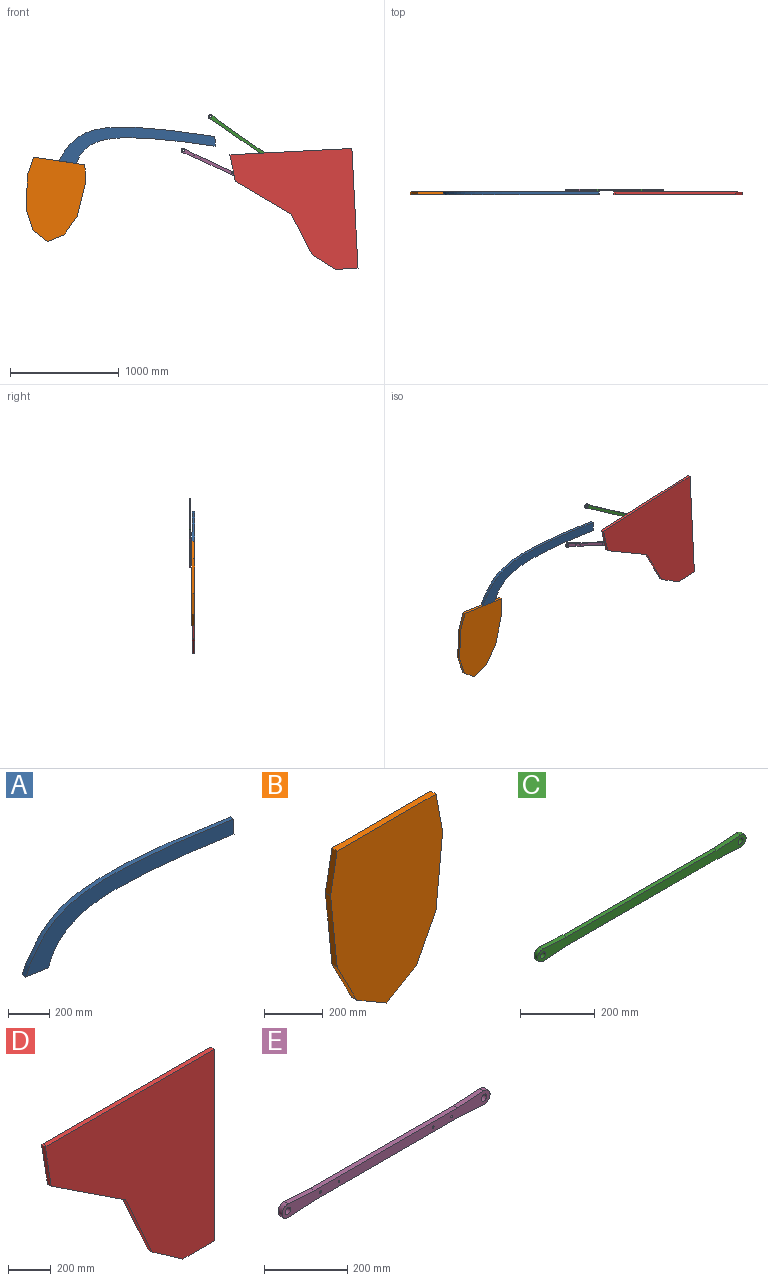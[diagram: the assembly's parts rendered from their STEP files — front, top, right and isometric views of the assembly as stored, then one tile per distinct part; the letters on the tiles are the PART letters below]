
ASSEMBLY  parts=5 mates=4
PART A: 7 faces, bbox 1432.8x25x381.3 mm
  f0: extruded ~999.54x237.45mm, area 27511.2mm2, adj f1,f4,f5,f6
  f1: extruded ~274.97x38.74mm, area 6942.4mm2, adj f0,f2,f5,f6
  f2: plane 90x25mm, normal (1,0,0), area 2250mm2, adj f1,f3,f5,f6
  f3: extruded ~1432.68x311.07mm, area 39088.2mm2, adj f2,f4,f5,f6
  f4: plane 158.25x25mm, normal (-0.15,0,-0.99), area 4000mm2, adj f0,f3,f5,f6
  f5: plane 1432.77x381.26mm, normal (0,-1,0), area 152801.9mm2, adj f0,f1,f2,f3,f4
  f6: plane 1432.77x381.26mm, normal (0,1,0), area 152801.9mm2, adj f0,f1,f2,f3,f4
PART B: 11 faces, bbox 538.6x25x751.3 mm
  f0: plane 475.91x25mm, normal (0,0,1), area 11897.7mm2, adj f1,f8,f9,f10
  f1: plane 170.47x31.37mm, normal (-0.98,0,0.18), area 4333.3mm2, adj f0,f2,f9,f10
  f2: plane 313.48x31.84mm, normal (-0.99,0,-0.1), area 7877.4mm2, adj f1,f3,f9,f10
  f3: plane 183.96x94.35mm, normal (-0.89,0,-0.46), area 5168.8mm2, adj f2,f4,f9,f10
  f4: plane 143.13x83.43mm, normal (-0.5,0,-0.86), area 4141.8mm2, adj f3,f5,f9,f10
  f5: plane 143.13x83.43mm, normal (0.5,0,-0.86), area 4141.8mm2, adj f4,f6,f9,f10
  f6: plane 183.96x94.35mm, normal (0.89,0,-0.46), area 5168.8mm2, adj f5,f7,f9,f10
  f7: plane 313.48x31.84mm, normal (0.99,0,-0.1), area 7877.4mm2, adj f6,f8,f9,f10
  f8: plane 170.47x31.37mm, normal (0.98,0,0.18), area 4333.3mm2, adj f0,f7,f9,f10
  f9: plane 751.35x538.64mm, normal (0,-1,0), area 327311.6mm2, adj f0,f1,f2,f3,f4,f5,f6,f7
  f10: plane 751.35x538.64mm, normal (0,1,0), area 327311.6mm2, adj f0,f1,f2,f3,f4,f5,f6,f7
PART C: 12 faces, bbox 790x14x40 mm
  f0: plane 88.77x14mm, normal (0.06,0,1), area 1245.2mm2, adj f1,f8,f10,f11
  f1: cylinder r=20mm len=40mm, axis (0,1,0), area 914.1mm2, adj f0,f2,f10,f11
  f2: plane 88.77x14mm, normal (0.06,0,-1), area 1245.2mm2, adj f1,f3,f10,f11
  f3: plane 570x14mm, normal (0,0,-1), area 7980mm2, adj f2,f4,f10,f11
  f4: plane 88.77x14mm, normal (-0.06,0,-1), area 1245.2mm2, adj f3,f5,f10,f11
  f5: cylinder r=20mm len=40mm, axis (0,1,0), area 914.1mm2, adj f4,f6,f10,f11
  f6: plane 88.77x14mm, normal (-0.06,0,1), area 1245.2mm2, adj f5,f8,f10,f11
  f7: cylinder r=9.5mm len=19mm, axis (0,1,0), area 835.7mm2, adj f10,f11
  f8: plane 570x14mm, normal (0,0,1), area 7980mm2, adj f0,f6,f10,f11
  f9: cylinder r=9.5mm len=19mm, axis (0,1,0), area 835.7mm2, adj f10,f11
  f10: plane 790x40mm, normal (0,-1,0), area 23436.3mm2, adj f0,f1,f2,f3,f4,f5,f6,f7
  f11: plane 790x40mm, normal (0,1,0), area 23436.3mm2, adj f0,f1,f2,f3,f4,f5,f6,f7
PART D: 14 faces, bbox 1125.3x50x1103.2 mm
  f0: plane 1112.1x25mm, normal (0,0,1), area 27802.5mm2, adj f1,f7,f8,f9
  f1: plane 25x13.25mm, normal (0.04,0,1), area 331.5mm2, adj f0,f2,f8,f9
  f2: plane 246.31x39.73mm, normal (-0.99,0,-0.16), area 6237.4mm2, adj f1,f3,f8,f9
  f3: plane 493.74x325.38mm, normal (-0.55,0,-0.83), area 14782.7mm2, adj f2,f4,f8,f9
  f4: plane 387.83x175.82mm, normal (-0.91,0,-0.41), area 10645.6mm2, adj f3,f5,f8,f9
  f5: plane 205.99x143.68mm, normal (-0.57,0,-0.82), area 6278.8mm2, adj f4,f6,f8,f9
  f6: plane 210.07x25mm, normal (0,0,-1), area 5251.8mm2, adj f5,f7,f8,f9
  f7: plane 1103.2x25mm, normal (1,0,0), area 27580.1mm2, adj f0,f6,f8,f9
  f8: plane 1125.35x1103.2mm, normal (0,-1,0), area 785366.9mm2, adj f0,f1,f2,f3,f4,f5,f6,f7
  f9: plane 1125.35x1103.2mm, normal (0,1,0), area 784799.8mm2, adj f0,f1,f2,f3,f4,f5,f6,f7
  f10: plane 19x19mm, normal (0,1,0), area 283.5mm2, adj f11
  f11: cylinder r=9.5mm len=25mm, axis (0,-1,0), area 1492.3mm2, adj f9,f10
  f12: plane 19x19mm, normal (0,1,0), area 283.5mm2, adj f13
  f13: cylinder r=9.5mm len=25mm, axis (0,-1,0), area 1492.3mm2, adj f9,f12
PART E: 16 faces, bbox 706.7x14x40 mm
  f0: plane 88.77x14mm, normal (0.06,0,1), area 1245.2mm2, adj f1,f12,f14,f15
  f1: cylinder r=20mm len=40mm, axis (0,1,0), area 914.1mm2, adj f0,f2,f14,f15
  f2: plane 88.77x14mm, normal (0.06,0,-1), area 1245.2mm2, adj f1,f3,f14,f15
  f3: plane 486.7x14mm, normal (0,0,-1), area 6813.8mm2, adj f2,f4,f14,f15
  f4: plane 88.77x14mm, normal (-0.06,0,-1), area 1245.2mm2, adj f3,f5,f14,f15
  f5: cylinder r=20mm len=40mm, axis (0,1,0), area 914.1mm2, adj f4,f6,f14,f15
  f6: plane 88.77x14mm, normal (-0.06,0,1), area 1245.2mm2, adj f5,f12,f14,f15
  f7: cylinder r=3.2mm len=14mm, axis (0,1,0), area 281.5mm2, adj f14,f15
  f8: cylinder r=3.2mm len=14mm, axis (0,1,0), area 281.5mm2, adj f14,f15
  f9: cylinder r=3.2mm len=14mm, axis (0,1,0), area 281.5mm2, adj f14,f15
  f10: cylinder r=3.2mm len=14mm, axis (0,1,0), area 281.5mm2, adj f14,f15
  f11: cylinder r=9.5mm len=19mm, axis (0,1,0), area 835.7mm2, adj f14,f15
  f12: plane 486.7x14mm, normal (0,0,1), area 6813.8mm2, adj f0,f6,f14,f15
  f13: cylinder r=9.5mm len=19mm, axis (0,1,0), area 835.7mm2, adj f14,f15
  f14: plane 706.7x40mm, normal (0,-1,0), area 20891.9mm2, adj f0,f1,f2,f3,f4,f5,f6,f7
  f15: plane 706.7x40mm, normal (0,1,0), area 20891.9mm2, adj f0,f1,f2,f3,f4,f5,f6,f7
PLACE A t=(0,57.54,0)mm
PLACE B rot(axis=(0,1,0),8.5deg) t=(-2523.72,57.54,183.3)mm
PLACE C rot(axis=(0,-1,0),145deg) t=(-716.55,75.54,1102.87)mm
PLACE D rot(axis=(0,-1,0),2.9deg) t=(332.46,57.54,-62.7)mm
PLACE E rot(axis=(0,-1,0),155deg) t=(-971.06,75.54,866.23)mm
MATE planar B.f9 <-> D.f8  axis (0,-1,0) through (-2463.45,32.54,587.96)mm
MATE revolute D.f11 <-> E.f1  axis (0,1,0) through (-668.94,82.54,725.35)mm
MATE slider B.f0 <-> A.f4  axis (0.15,0,0.99) through (-2415.25,45.04,911.57)mm
MATE revolute C.f1 <-> D.f13  axis (0,1,0) through (-409.37,82.54,887.77)mm
